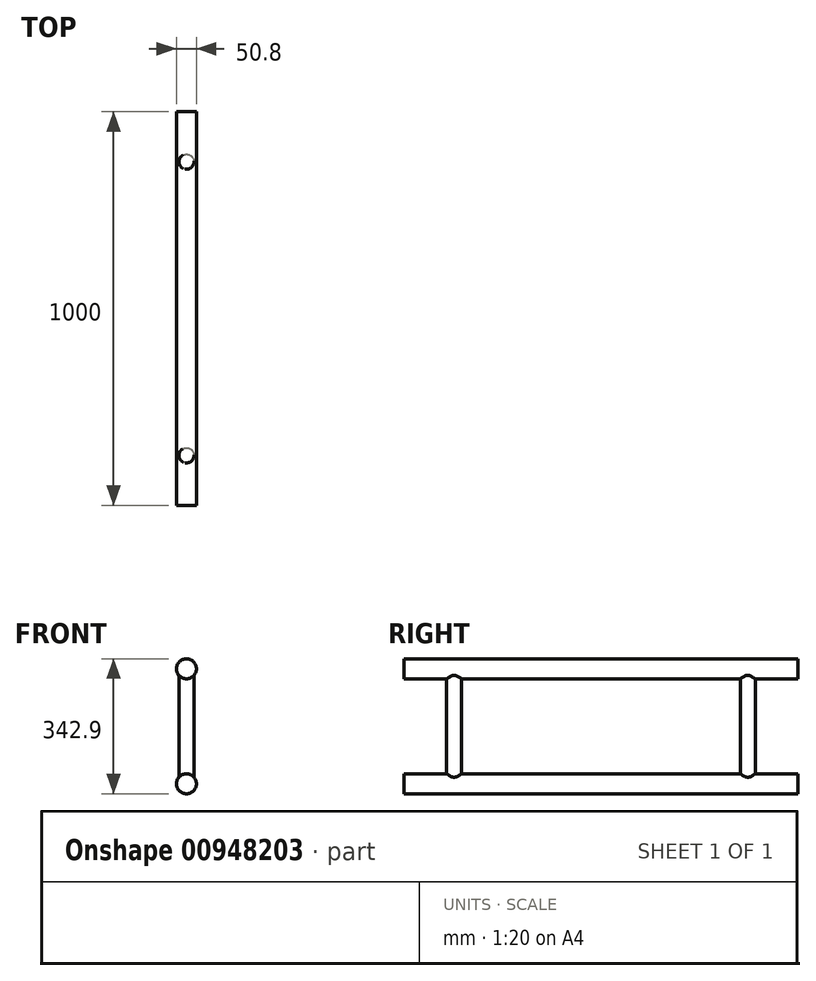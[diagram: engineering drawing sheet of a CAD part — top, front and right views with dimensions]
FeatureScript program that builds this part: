
annotation { "Feature Type Name" : "Feature", "Feature Type Description" : "" }
export const myFeature = defineFeature(function(context is Context, id is Id, definition is map)
    precondition{}
    {
        {
            var Q0;
            Q0=qCreatedBy(makeId("Front.planeOp"),FACE);
            cPlane(context, id + "F0", {"entities" : qUnion([Q0]), "cplaneType" : CPlaneType.OFFSET, "offset" : 1000 * mm, "oppositeDirection" : true, "width" : 150 * mm, "height" : 150 * mm});
        }
        {
            var Q0;
            Q0=qCreatedBy(makeId("Front.planeOp"),FACE);
            var sketch = newSketch(context, id + "F1", { "sketchPlane" : qUnion([Q0])});
            skCircle(sketch, "E0", {"center": v(0, 0) * mm, "radius": 25.4 * mm});
            skPoint(sketch, "E1", {"position": v(0, 292.1) * mm});
            skCircle(sketch, "E2", {"center": v(0, 292.1) * mm, "radius": 25.4 * mm});
            skSolve(sketch);
        }
        {
            var Q0;
            Q0=makeQuery(id+"F1.imprint","IMPRINT",FACE,{"disambiguationData":[TD([[makeQuery(id+"F1.imprint","IMPRINT",EDGE,{"derivedFrom":sQuery(id+"F1.wireOp",EDGE,"E2")}),1.0]])]});
            var Q1;
            Q1=makeQuery(id+"F1.imprint","IMPRINT",FACE,{"disambiguationData":[TD([[makeQuery(id+"F1.imprint","IMPRINT",EDGE,{"derivedFrom":sQuery(id+"F1.wireOp",EDGE,"E0")}),1.0]])]});
            var Q2;
            Q2=qCreatedBy(id+"F0.planeOp",FACE);
            extrude(context, id + "F2", {"entities" : qUnion([Q0, Q1]), "endBound" : BoundingType.UP_TO_SURFACE, "oppositeDirection" : true, "depth" : 25.4 * mm, "endBoundEntityFace" : qUnion([Q2]), "offsetDistance" : 25.4 * mm});
        }
        {
            var Q0;
            Q0=qCreatedBy(makeId("Top.planeOp"),FACE);
            var sketch = newSketch(context, id + "F3", { "sketchPlane" : qUnion([Q0])});
            skLineSegment(sketch, "E3.0", {"start": v(-25.4, 1000) * mm, "end": v(25.4, 1000) * mm, "construction": true});
            skLineSegment(sketch, "E4", {"start": v(0, 0) * mm, "end": v(0, 1000) * mm, "construction": true});
            skPoint(sketch, "E5", {"position": v(0, 127) * mm});
            skPoint(sketch, "E6", {"position": v(0, 873) * mm});
            skCircle(sketch, "E7", {"center": v(0, 127) * mm, "radius": 19.05 * mm});
            skCircle(sketch, "E8", {"center": v(0, 873) * mm, "radius": 19.05 * mm});
            skSolve(sketch);
        }
        {
            var Q0;
            Q0=makeQuery(id+"F3.imprint","IMPRINT",FACE,{"disambiguationData":[TD([[makeQuery(id+"F3.imprint","IMPRINT",EDGE,{"derivedFrom":sQuery(id+"F3.wireOp",EDGE,"E8")}),1.0]])]});
            var Q1;
            Q1=makeQuery(id+"F3.imprint","IMPRINT",FACE,{"disambiguationData":[TD([[makeQuery(id+"F3.imprint","IMPRINT",EDGE,{"derivedFrom":sQuery(id+"F3.wireOp",EDGE,"E7")}),1.0]])]});
            var Q2;
            Q2=makeQuery(id+"F2.opExtrude","SWEPT_BODY",BODY,{"disambiguationData":[OSD([sQuery(id+"F1.wireOp",EDGE,"E2")])]});
            extrude(context, id + "F4", {"entities" : qUnion([Q0, Q1]), "operationType" : NewBodyOperationType.ADD, "endBound" : BoundingType.UP_TO_BODY, "depth" : 25.4 * mm, "endBoundEntityBody" : qUnion([Q2]), "offsetDistance" : 25.4 * mm});
        }
    });
